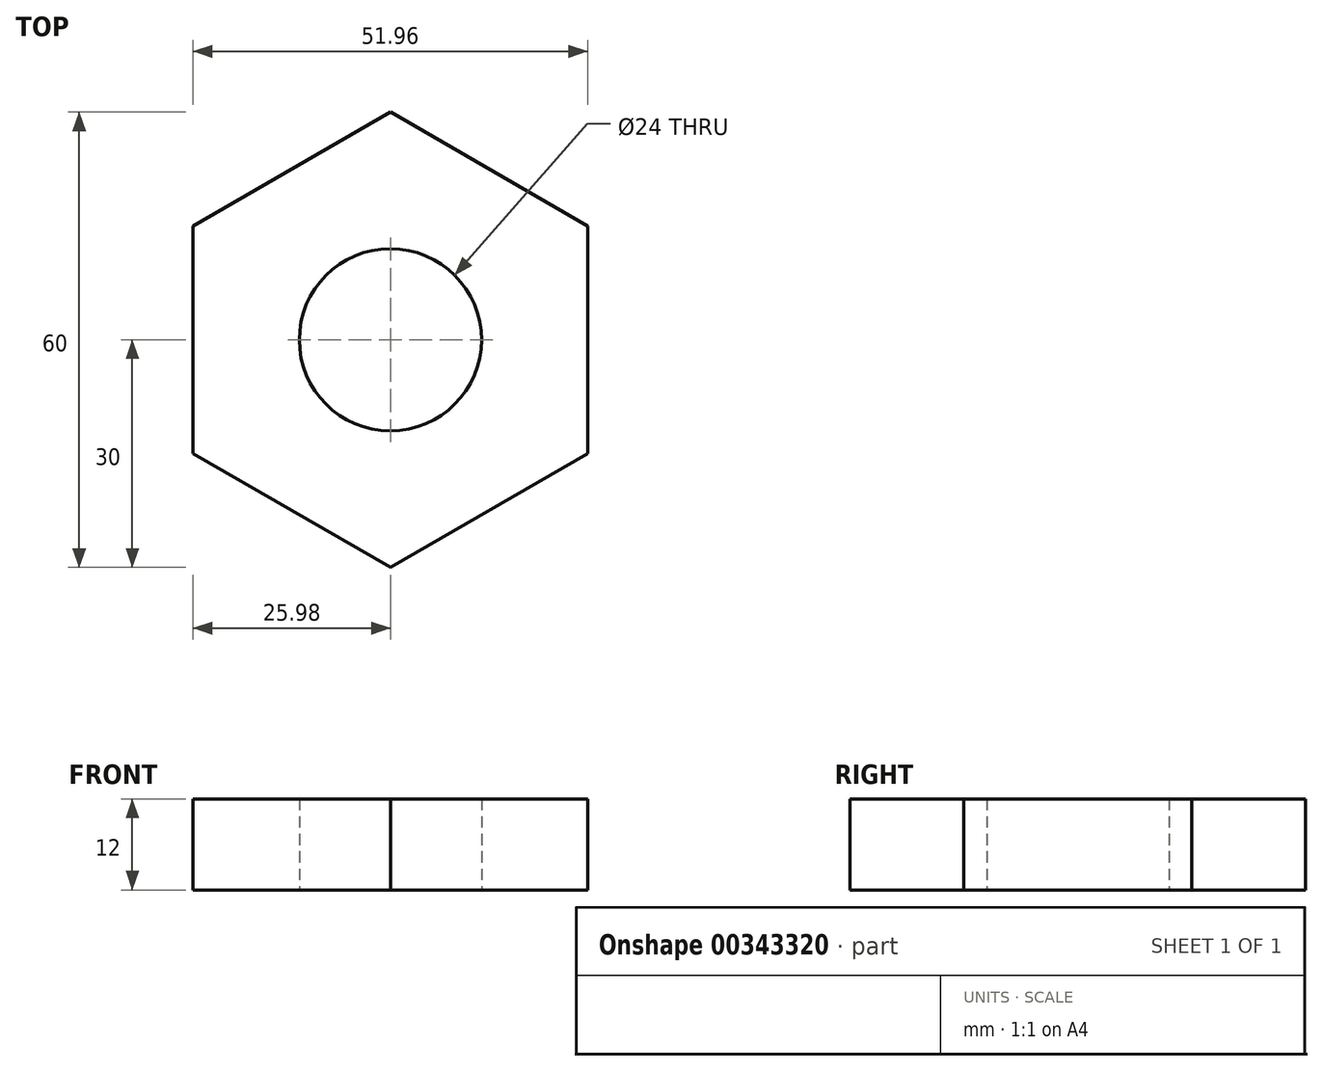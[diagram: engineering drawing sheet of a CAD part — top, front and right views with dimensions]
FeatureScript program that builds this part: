
annotation { "Feature Type Name" : "Feature", "Feature Type Description" : "" }
export const myFeature = defineFeature(function(context is Context, id is Id, definition is map)
    precondition{}
    {
        {
            var Q0;
            Q0=qCreatedBy(makeId("Top.planeOp"),FACE);
            var sketch = newSketch(context, id + "F0", { "sketchPlane" : qUnion([Q0])});
            skLineSegment(sketch, "E0.0", {"start": v(0, 30) * mm, "end": v(25.98, 15) * mm});
            skLineSegment(sketch, "E0.1", {"start": v(25.98, 15) * mm, "end": v(25.98, -15) * mm});
            skLineSegment(sketch, "E0.2", {"start": v(25.98, -15) * mm, "end": v(0, -30) * mm});
            skLineSegment(sketch, "E0.3", {"start": v(0, -30) * mm, "end": v(-25.98, -15) * mm});
            skLineSegment(sketch, "E0.4", {"start": v(-25.98, -15) * mm, "end": v(-25.98, 15) * mm});
            skLineSegment(sketch, "E0.5", {"start": v(-25.98, 15) * mm, "end": v(0, 30) * mm});
            skCircle(sketch, "E1", {"center": v(0, 0) * mm, "radius": 12 * mm});
            skSolve(sketch);
        }
        {
            var Q0;
            Q0 = qSketchRegion(id + "F0", true);
            var Q1;
            Q1=makeQuery(id+"F0.imprint","IMPRINT",FACE,{"disambiguationData":[TD([[makeQuery(id+"F0.imprint","IMPRINT",EDGE,{"derivedFrom":sQuery(id+"F0.wireOp",EDGE,"E0.0")}),-1.0]])]});
            extrude(context, id + "F1", {"entities" : qUnion([Q0, Q1]), "depth" : 12 * mm});
        }
    });
